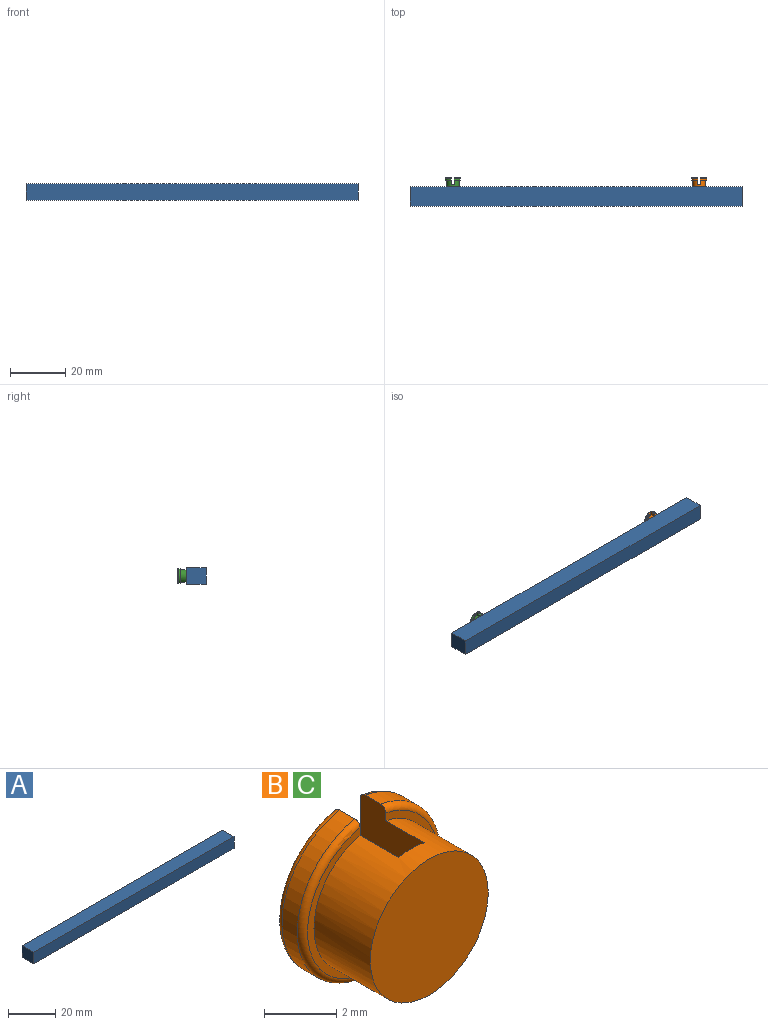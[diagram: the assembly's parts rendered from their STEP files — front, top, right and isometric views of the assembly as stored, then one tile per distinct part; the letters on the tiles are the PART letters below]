
ASSEMBLY  parts=3 mates=2
PART A: 6 faces, bbox 120x7x6 mm
  f0: plane 120x7mm, normal (0,0,1), area 840mm2, adj f1,f3,f4,f5
  f1: plane 7x6mm, normal (-1,0,0), area 42mm2, adj f0,f2,f4,f5
  f2: plane 120x7mm, normal (0,0,-1), area 840mm2, adj f1,f3,f4,f5
  f3: plane 7x6mm, normal (1,0,0), area 42mm2, adj f0,f2,f4,f5
  f4: plane 120x6mm, normal (0,-1,0), area 720mm2, adj f0,f1,f2,f3
  f5: plane 120x6mm, normal (0,1,0), area 720mm2, adj f0,f1,f2,f3
PART B: 15 faces, bbox 6x3.2x5.9 mm
  f0: cylinder r=2.75mm len=5.41mm, axis (0,1,0), area 4.6mm2, adj f9,f13,f14
  f1: plane 5x2.05mm, normal (0,-1,0), area 1.7mm2, adj f6,f9,f13
  f2: plane 5x2.05mm, normal (0,1,0), area 7.7mm2, adj f8,f11
  f3: cylinder r=2.75mm len=5.41mm, axis (0,1,0), area 4.6mm2, adj f8,f11,f12
  f4: plane 5x2.05mm, normal (0,-1,0), area 1.7mm2, adj f6,f8,f12
  f5: plane 5x2.05mm, normal (0,1,0), area 7.7mm2, adj f9,f14
  f6: cylinder r=2.3mm len=4.6mm, axis (0,1,0), area 28.8mm2, adj f1,f4,f7,f8,f9,f10
  f7: plane 4.6x4.6mm, normal (0,-1,0), area 16.6mm2, adj f6
  f8: plane 5.43x2.52mm, normal (-1,0,0), area 12.1mm2, adj f2,f3,f4,f6,f10,f11,f12
  f9: plane 5.43x2.52mm, normal (1,0,0), area 12.1mm2, adj f0,f1,f5,f6,f10,f13,f14
  f10: plane 4.6x1mm, normal (0,1,0), area 4.6mm2, adj f6,f8,f9
  f11: torus R=2.55mm, axis (0,-1,0), area 2.3mm2, adj f2,f3,f8
  f12: torus R=2.55mm, axis (0,-1,0), area 2.3mm2, adj f3,f4,f8
  f13: torus R=2.55mm, axis (0,-1,0), area 2.3mm2, adj f0,f1,f9
  f14: torus R=2.55mm, axis (0,-1,0), area 2.3mm2, adj f0,f5,f9
PART C: same geometry as B
PLACE A t=(-65.48,-2.69,15.84)mm
PLACE B t=(62.23,0.51,-21.43)mm
PLACE C t=(-26.77,0.51,-21.43)mm
MATE fastened C.f0 <-> A.f5  axis (0,-1,0) through (-74.16,-2.69,16.4)mm
MATE fastened B.f0 <-> A.f5  axis (0,-1,0) through (14.84,-2.69,16.4)mm
